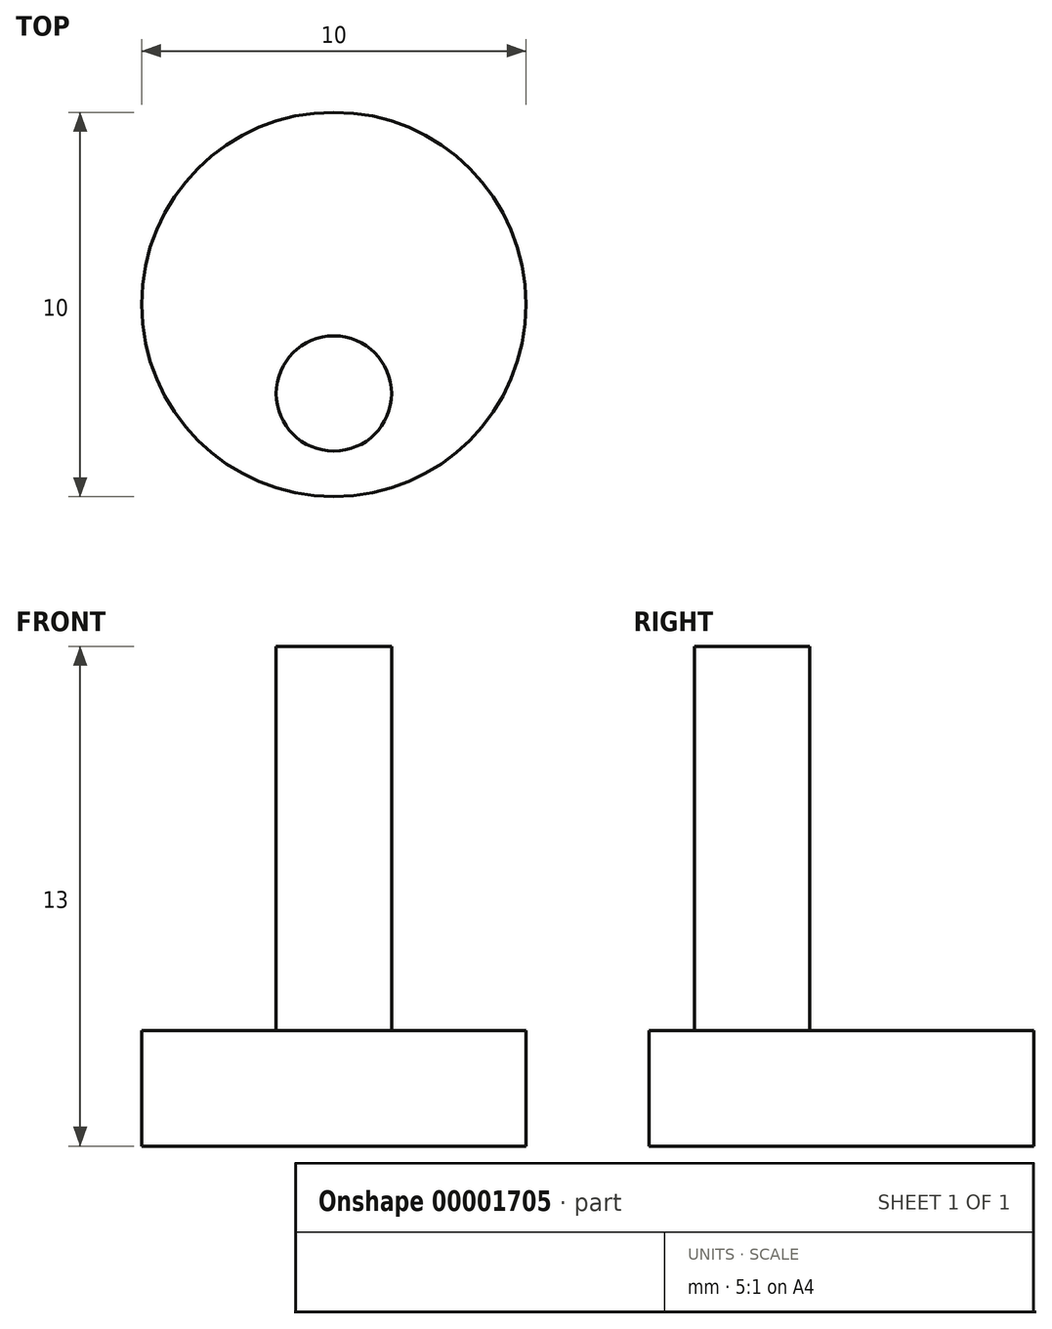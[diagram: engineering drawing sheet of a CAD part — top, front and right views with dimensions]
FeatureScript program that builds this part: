
annotation { "Feature Type Name" : "Feature", "Feature Type Description" : "" }
export const myFeature = defineFeature(function(context is Context, id is Id, definition is map)
    precondition{}
    {
        {
            var Q0;
            Q0=qCreatedBy(makeId("Top.planeOp"),FACE);
            var sketch = newSketch(context, id + "F0", { "sketchPlane" : qUnion([Q0])});
            skCircle(sketch, "E0", {"center": v(0, 0) * mm, "radius": 5 * mm});
            skSolve(sketch);
        }
        {
            var Q0;
            Q0=makeQuery(id+"F0.imprint","IMPRINT",FACE,{"disambiguationData":[TD([[makeQuery(id+"F0.imprint","IMPRINT",EDGE,{"derivedFrom":sQuery(id+"F0.wireOp",EDGE,"E0")}),1.0]])]});
            extrude(context, id + "F1", {"entities" : qUnion([Q0]), "depth" : 3 * mm});
        }
        {
            var Q0;
            Q0=makeQuery(id+"F1.opExtrude","CAP_FACE",FACE,{"disambiguationData":[OSD([sQuery(id+"F0.wireOp",EDGE,"E0")])],"isStart":false});
            var sketch = newSketch(context, id + "F2", { "sketchPlane" : qUnion([Q0])});
            skCircle(sketch, "E1", {"center": v(0, -2.32) * mm, "radius": 1.5 * mm});
            skSolve(sketch);
        }
        {
            var Q0;
            Q0=makeQuery(id+"F2.imprint","IMPRINT",FACE,{"disambiguationData":[TD([[makeQuery(id+"F2.imprint","IMPRINT",EDGE,{"derivedFrom":sQuery(id+"F2.wireOp",EDGE,"E1")}),1.0]])]});
            extrude(context, id + "F3", {"entities" : qUnion([Q0]), "operationType" : NewBodyOperationType.ADD, "depth" : 10 * mm});
        }
    });
